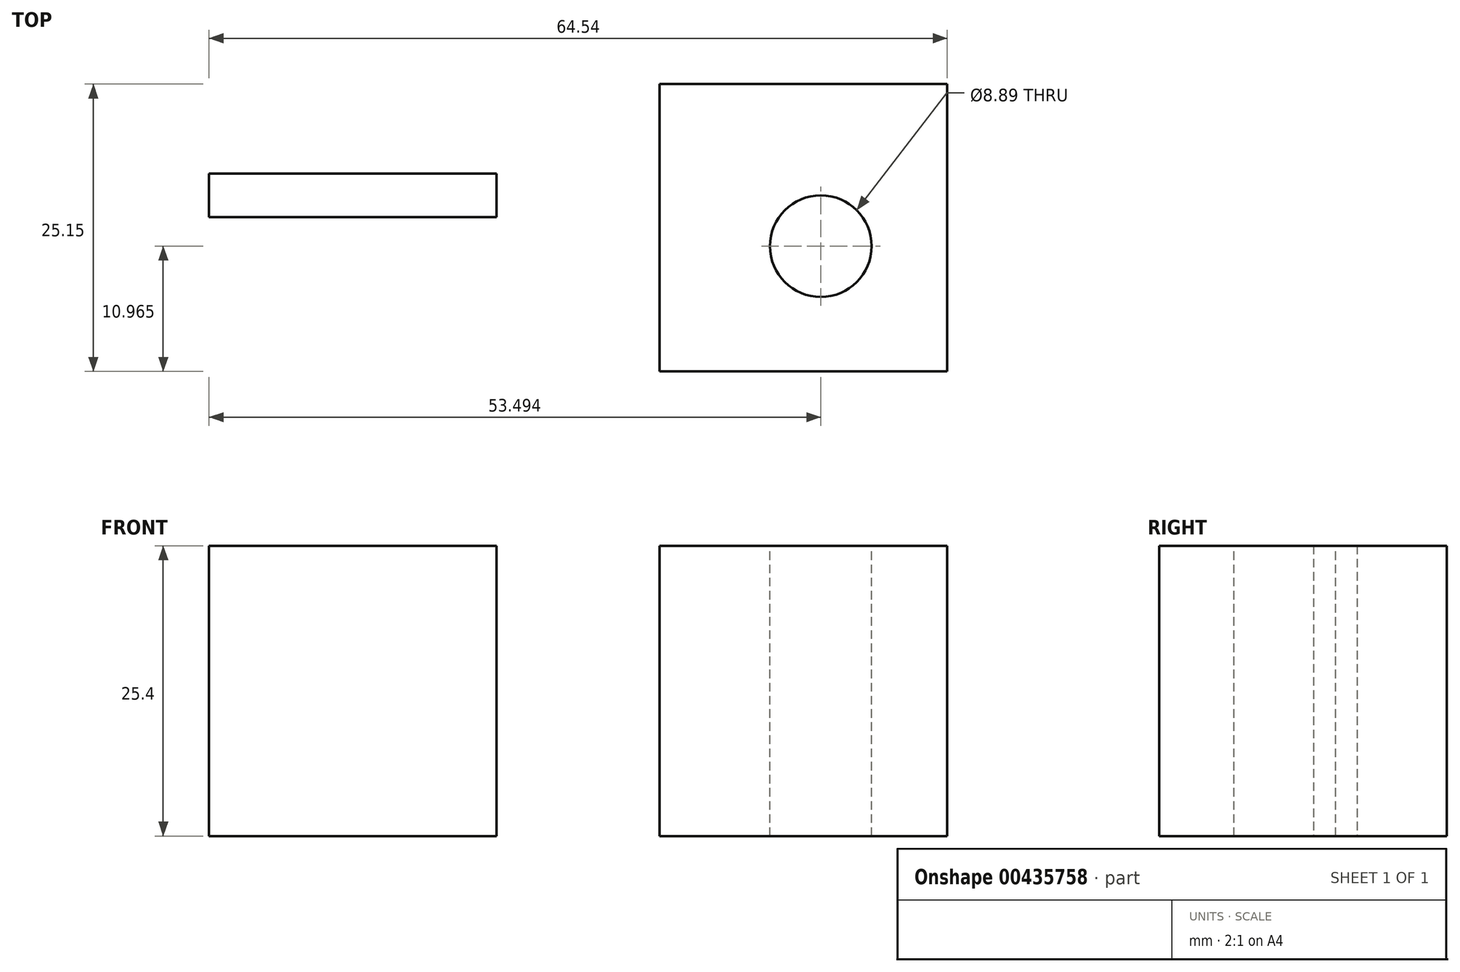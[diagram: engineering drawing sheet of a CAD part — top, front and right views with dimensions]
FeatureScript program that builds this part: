
annotation { "Feature Type Name" : "Feature", "Feature Type Description" : "" }
export const myFeature = defineFeature(function(context is Context, id is Id, definition is map)
    precondition{}
    {
        {
            var Q0;
            Q0=qCreatedBy(makeId("Top.planeOp"),FACE);
            var sketch = newSketch(context, id + "F0", { "sketchPlane" : qUnion([Q0])});
            skLineSegment(sketch, "E0.bottom", {"start": v(-10.81, 11.2) * mm, "end": v(14.34, 11.2) * mm});
            skLineSegment(sketch, "E0.top", {"start": v(-10.81, -13.95) * mm, "end": v(14.34, -13.95) * mm});
            skLineSegment(sketch, "E0.left", {"start": v(-10.81, 11.2) * mm, "end": v(-10.81, -13.95) * mm});
            skLineSegment(sketch, "E0.right", {"start": v(14.34, 11.2) * mm, "end": v(14.34, -13.95) * mm});
            skSolve(sketch);
        }
        {
            var Q0;
            Q0=makeQuery(id+"F0.imprint","IMPRINT",FACE,{"disambiguationData":[TD([[makeQuery(id+"F0.imprint","IMPRINT",EDGE,{"derivedFrom":sQuery(id+"F0.wireOp",EDGE,"E0.bottom")}),-1.0]])]});
            extrude(context, id + "F1", {"entities" : qUnion([Q0]), "depth" : 25.4 * mm});
        }
        {
            var Q0;
            Q0=makeQuery(id+"F1.opExtrude","CAP_FACE",FACE,{"disambiguationData":[OSD([sQuery(id+"F0.wireOp",EDGE,"E0.bottom"),sQuery(id+"F0.wireOp",EDGE,"E0.top"),sQuery(id+"F0.wireOp",EDGE,"E0.left"),sQuery(id+"F0.wireOp",EDGE,"E0.right")])],"isStart":false});
            var sketch = newSketch(context, id + "F2", { "sketchPlane" : qUnion([Q0])});
            skCircle(sketch, "E1", {"center": v(3.3, -2.98) * mm, "radius": 4.45 * mm});
            skSolve(sketch);
        }
        {
            var Q0;
            Q0=makeQuery(id+"F2.imprint","IMPRINT",FACE,{"disambiguationData":[TD([[makeQuery(id+"F2.imprint","IMPRINT",EDGE,{"derivedFrom":sQuery(id+"F2.wireOp",EDGE,"E1")}),1.0]])]});
            var Q1;
            Q1=sQuery(id+"F2.wireOp",EDGE,"E1");
            extrude(context, id + "F3", {"entities" : qUnion([Q0]), "operationType" : NewBodyOperationType.REMOVE, "surfaceEntities" : qUnion([Q1]), "oppositeDirection" : true, "depth" : 25.4 * mm});
        }
        {
            var Q0;
            Q0=qCreatedBy(makeId("Top.planeOp"),FACE);
            var sketch = newSketch(context, id + "F4", { "sketchPlane" : qUnion([Q0])});
            skLineSegment(sketch, "E2.bottom", {"start": v(-50.2, 3.35) * mm, "end": v(-25.06, 3.35) * mm});
            skLineSegment(sketch, "E2.top", {"start": v(-50.2, -0.46) * mm, "end": v(-25.06, -0.46) * mm});
            skLineSegment(sketch, "E2.left", {"start": v(-50.2, 3.35) * mm, "end": v(-50.2, -0.46) * mm});
            skLineSegment(sketch, "E2.right", {"start": v(-25.06, 3.35) * mm, "end": v(-25.06, -0.46) * mm});
            skSolve(sketch);
        }
        {
            var Q0;
            Q0=makeQuery(id+"F4.imprint","IMPRINT",FACE,{"disambiguationData":[TD([[makeQuery(id+"F4.imprint","IMPRINT",EDGE,{"derivedFrom":sQuery(id+"F4.wireOp",EDGE,"E2.bottom")}),-1.0]])]});
            extrude(context, id + "F5", {"entities" : qUnion([Q0]), "depth" : 25.4 * mm});
        }
    });
